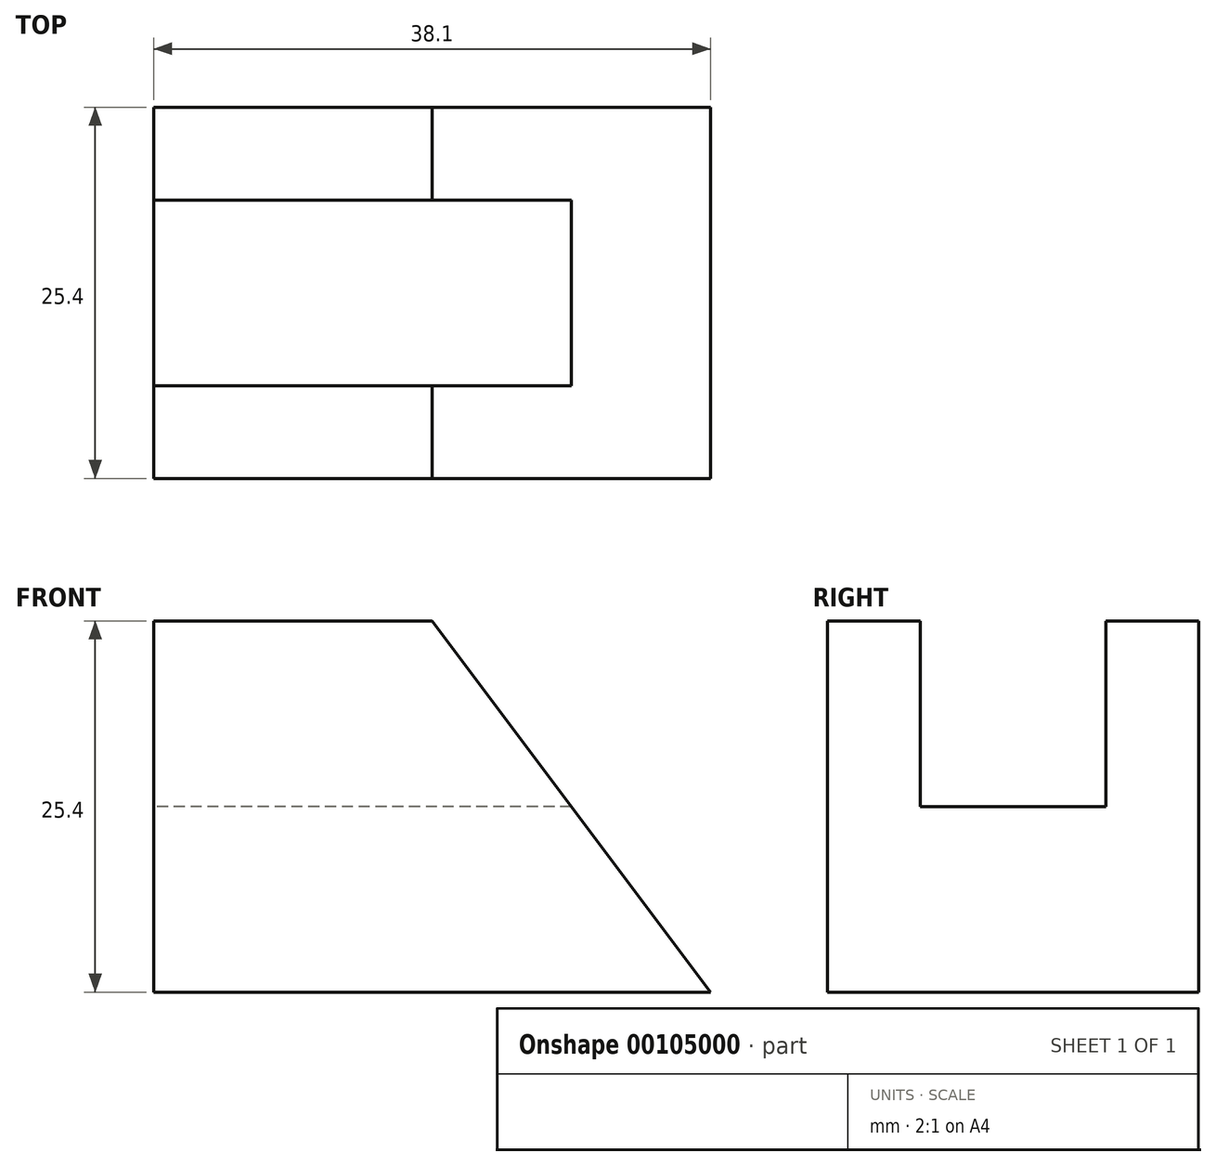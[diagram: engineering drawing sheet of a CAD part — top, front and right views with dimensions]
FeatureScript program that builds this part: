
annotation { "Feature Type Name" : "Feature", "Feature Type Description" : "" }
export const myFeature = defineFeature(function(context is Context, id is Id, definition is map)
    precondition{}
    {
        {
            var Q0;
            Q0=qCreatedBy(makeId("Front.planeOp"),FACE);
            var sketch = newSketch(context, id + "F0", { "sketchPlane" : qUnion([Q0])});
            skLineSegment(sketch, "E0.bottom", {"start": v(0, 0) * mm, "end": v(38.1, 0) * mm});
            skLineSegment(sketch, "E0.top", {"start": v(0, 25.4) * mm, "end": v(19.05, 25.4) * mm});
            skLineSegment(sketch, "E0.left", {"start": v(0, 0) * mm, "end": v(0, 25.4) * mm});
            skLineSegment(sketch, "E1", {"start": v(19.05, 25.4) * mm, "end": v(38.1, 0) * mm});
            skSolve(sketch);
        }
        {
            var Q0;
            Q0=makeQuery(id+"F0.imprint","IMPRINT",FACE,{"disambiguationData":[TD([[makeQuery(id+"F0.imprint","IMPRINT",EDGE,{"derivedFrom":sQuery(id+"F0.wireOp",EDGE,"E0.bottom")}),1.0]])]});
            extrude(context, id + "F1", {"entities" : qUnion([Q0]), "endBound" : BoundingType.SYMMETRIC, "depth" : 25.4 * mm});
        }
        {
            var Q0;
            Q0=makeQuery(id+"F1.opExtrude","SWEPT_FACE",FACE,{"disambiguationData":[OSD([sQuery(id+"F0.wireOp",EDGE,"E0.left")])]});
            var sketch = newSketch(context, id + "F2", { "sketchPlane" : qUnion([Q0])});
            skLineSegment(sketch, "E2.bottom", {"start": v(-6.35, 25.4) * mm, "end": v(6.35, 25.4) * mm});
            skLineSegment(sketch, "E2.top", {"start": v(-6.35, 12.7) * mm, "end": v(6.35, 12.7) * mm});
            skLineSegment(sketch, "E2.left", {"start": v(-6.35, 25.4) * mm, "end": v(-6.35, 12.7) * mm});
            skLineSegment(sketch, "E2.right", {"start": v(6.35, 25.4) * mm, "end": v(6.35, 12.7) * mm});
            skSolve(sketch);
        }
        {
            var Q0;
            Q0=makeQuery(id+"F2.imprint","IMPRINT",FACE,{"disambiguationData":[TD([[makeQuery(id+"F2.imprint","IMPRINT",EDGE,{"derivedFrom":sQuery(id+"F2.wireOp",EDGE,"E2.bottom")}),1.0]])]});
            extrude(context, id + "F3", {"entities" : qUnion([Q0]), "operationType" : NewBodyOperationType.REMOVE, "endBound" : BoundingType.THROUGH_ALL, "oppositeDirection" : true, "depth" : 25.4 * mm});
        }
    });
